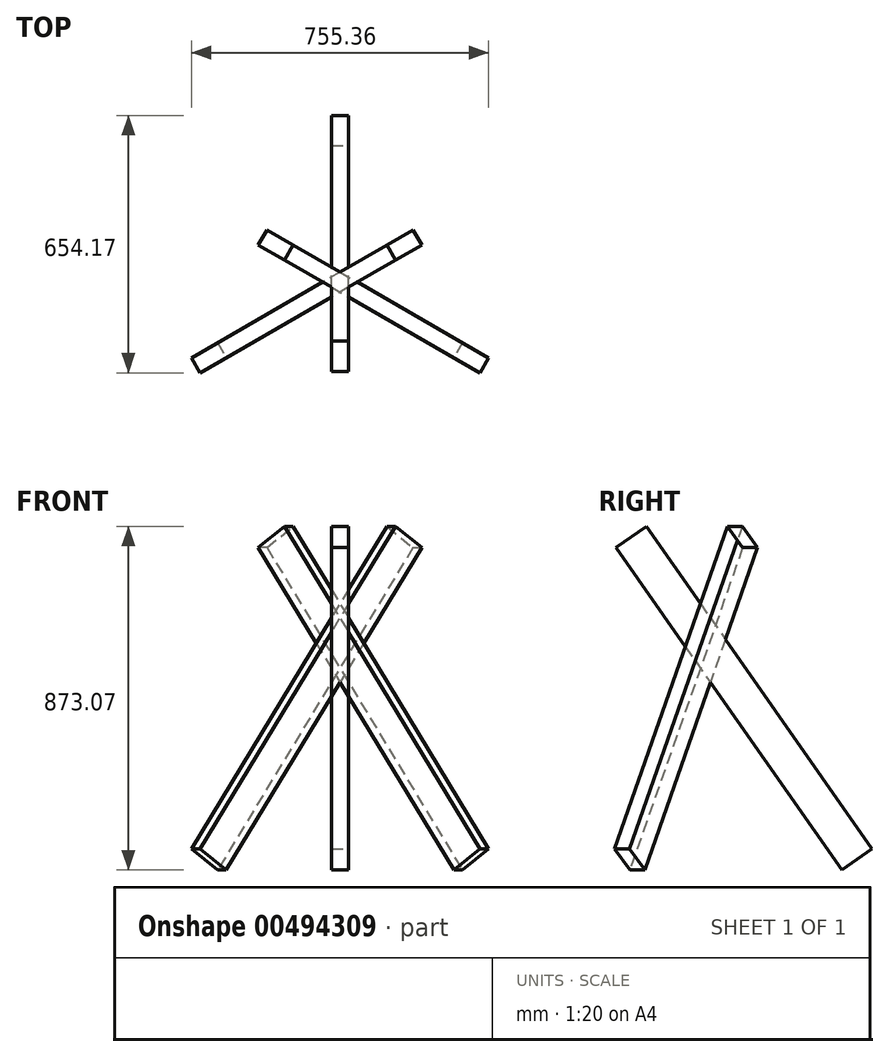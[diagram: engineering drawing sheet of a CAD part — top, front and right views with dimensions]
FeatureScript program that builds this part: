
annotation { "Feature Type Name" : "Feature", "Feature Type Description" : "" }
export const myFeature = defineFeature(function(context is Context, id is Id, definition is map)
    precondition{}
    {
        {
            var Q0;
            Q0=qCreatedBy(makeId("Top.planeOp"),FACE);
            var sketch = newSketch(context, id + "F0", { "sketchPlane" : qUnion([Q0])});
            skLineSegment(sketch, "E0", {"start": v(0, 0) * mm, "end": v(600, 0) * mm});
            skLineSegment(sketch, "E1", {"start": v(600, 0) * mm, "end": v(300, 519.62) * mm});
            skLineSegment(sketch, "E2", {"start": v(300, 519.62) * mm, "end": v(0, 0) * mm});
            skLineSegment(sketch, "E3.bottom", {"start": v(278, 519.62) * mm, "end": v(322, 519.62) * mm});
            skLineSegment(sketch, "E3.top", {"start": v(278, 613.62) * mm, "end": v(322, 613.62) * mm});
            skLineSegment(sketch, "E3.left", {"start": v(278, 519.62) * mm, "end": v(278, 613.62) * mm});
            skLineSegment(sketch, "E3.right", {"start": v(322, 519.62) * mm, "end": v(322, 613.62) * mm});
            skLineSegment(sketch, "E4.bottom", {"start": v(611, 19.05) * mm, "end": v(692.4, -27.95) * mm});
            skLineSegment(sketch, "E4.top", {"start": v(589, -19.05) * mm, "end": v(670.4, -66.05) * mm});
            skLineSegment(sketch, "E4.left", {"start": v(611, 19.05) * mm, "end": v(589, -19.05) * mm});
            skLineSegment(sketch, "E4.right", {"start": v(692.4, -27.95) * mm, "end": v(670.4, -66.05) * mm});
            skLineSegment(sketch, "E5.bottom", {"start": v(-92.4, -27.95) * mm, "end": v(-11, 19.05) * mm});
            skLineSegment(sketch, "E5.top", {"start": v(-70.4, -66.05) * mm, "end": v(11, -19.05) * mm});
            skLineSegment(sketch, "E5.left", {"start": v(-92.4, -27.95) * mm, "end": v(-70.4, -66.05) * mm});
            skLineSegment(sketch, "E5.right", {"start": v(-11, 19.05) * mm, "end": v(11, -19.05) * mm});
            skSolve(sketch);
        }
        {
            var Q0;
            Q0=makeQuery(id+"F0.imprint","IMPRINT",FACE,{"disambiguationData":[TD([[makeQuery(id+"F0.imprint","IMPRINT",EDGE,{"derivedFrom":sQuery(id+"F0.wireOp",EDGE,"E3.top")}),-1.0]])]});
            var Q1;
            {var subQ3=sQuery(id+"F0.wireOp",EDGE,"E4.bottom");Q1=makeQuery(id+"F0.imprint","IMPRINT",FACE,{"disambiguationData":[TD([[makeQuery(id+"F0.imprint","IMPRINT",EDGE,{"derivedFrom":subQ3}),-1.0]])]});}
            var Q2;
            {var subQ2=sQuery(id+"F0.wireOp",EDGE,"E5.bottom");Q2=makeQuery(id+"F0.imprint","IMPRINT",FACE,{"disambiguationData":[TD([[makeQuery(id+"F0.imprint","IMPRINT",EDGE,{"derivedFrom":subQ2}),-1.0]])]});}
            extrude(context, id + "F1", {"entities" : qUnion([Q0, Q1, Q2]), "depth" : 1000 * mm, "offsetDistance" : 25 * mm});
        }
        {
            var Q0;
            Q0=makeQuery(id+"F1.opExtrude","SWEPT_BODY",BODY,{"disambiguationData":[OSD([sQuery(id+"F0.wireOp",EDGE,"E3.bottom"),sQuery(id+"F0.wireOp",EDGE,"E3.top"),sQuery(id+"F0.wireOp",EDGE,"E3.left"),sQuery(id+"F0.wireOp",EDGE,"E3.right")])]});
            var Q1;
            Q1=sQuery(id+"F0.wireOp",EDGE,"E3.bottom");
            transform(context, id + "F2", {"entities" : qUnion([Q0]), "transformType" : TransformType.ROTATION, "transformAxis" : qUnion([Q1]), "angle" : 35 * degree, "makeCopy" : false});
        }
        {
            var Q0;
            Q0=makeQuery(id+"F1.opExtrude","SWEPT_BODY",BODY,{"disambiguationData":[OSD([sQuery(id+"F0.wireOp",EDGE,"E5.bottom"),sQuery(id+"F0.wireOp",EDGE,"E5.top"),sQuery(id+"F0.wireOp",EDGE,"E5.left"),sQuery(id+"F0.wireOp",EDGE,"E5.right")])]});
            var Q1;
            Q1=sQuery(id+"F0.wireOp",EDGE,"E5.right");
            transform(context, id + "F3", {"entities" : qUnion([Q0]), "transformType" : TransformType.ROTATION, "transformAxis" : qUnion([Q1]), "angle" : 35 * degree, "oppositeDirection" : true, "makeCopy" : false});
        }
        {
            var Q0;
            Q0=makeQuery(id+"F1.opExtrude","SWEPT_BODY",BODY,{"disambiguationData":[OSD([sQuery(id+"F0.wireOp",EDGE,"E4.bottom"),sQuery(id+"F0.wireOp",EDGE,"E4.top"),sQuery(id+"F0.wireOp",EDGE,"E4.left"),sQuery(id+"F0.wireOp",EDGE,"E4.right")])]});
            var Q1;
            Q1=sQuery(id+"F0.wireOp",EDGE,"E4.left");
            transform(context, id + "F4", {"entities" : qUnion([Q0]), "transformType" : TransformType.ROTATION, "transformAxis" : qUnion([Q1]), "angle" : 35 * degree, "makeCopy" : false});
        }
    });
